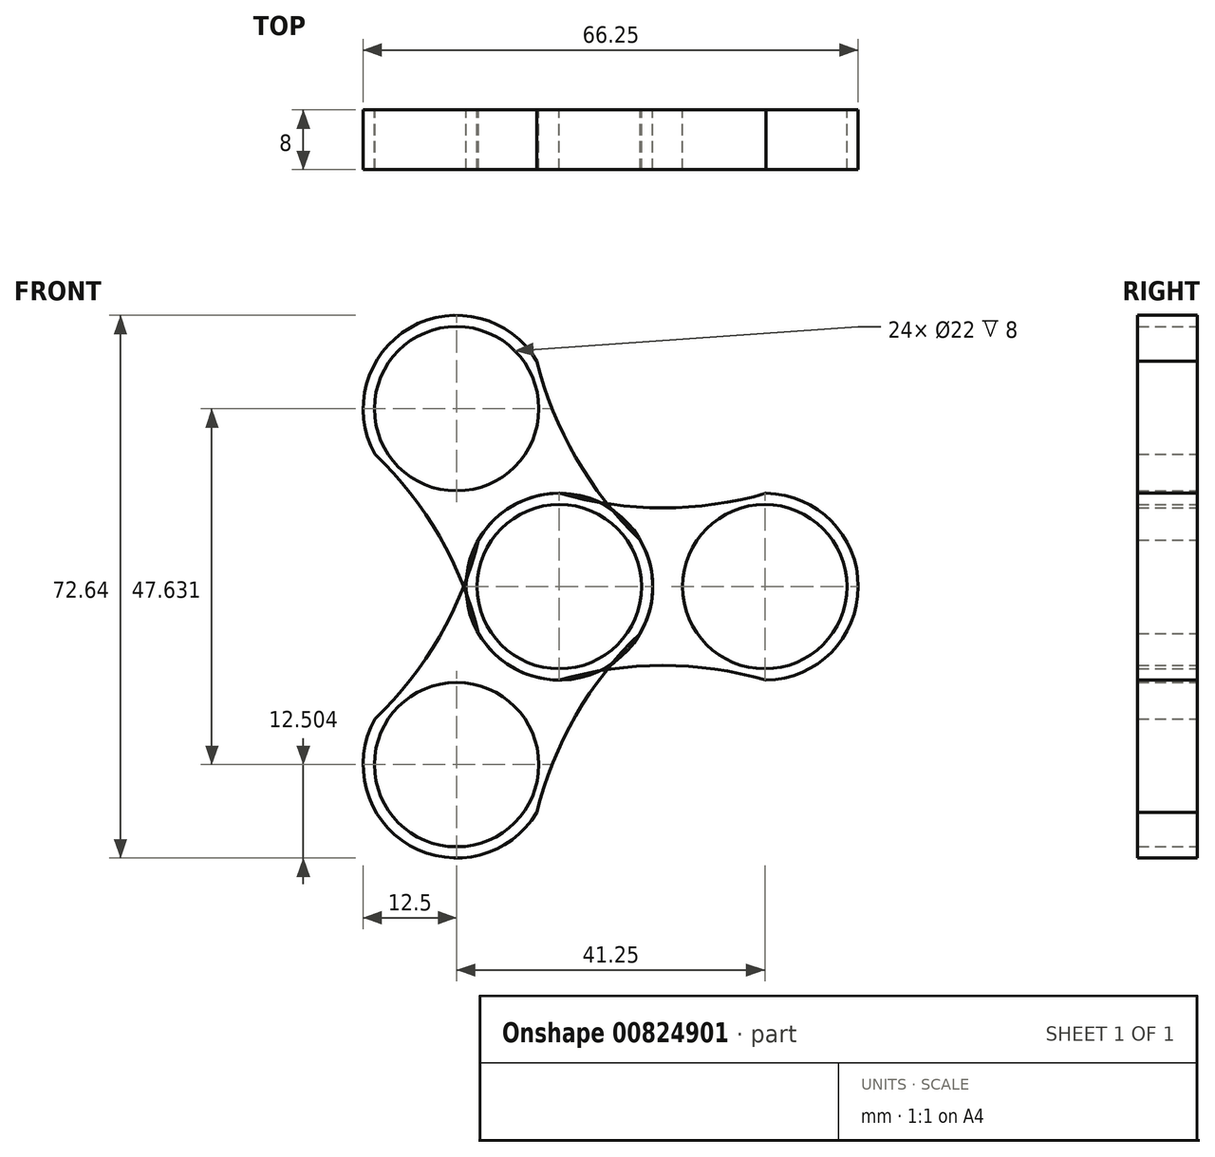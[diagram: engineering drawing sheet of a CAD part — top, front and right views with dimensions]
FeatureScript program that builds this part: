
annotation { "Feature Type Name" : "Feature", "Feature Type Description" : "" }
export const myFeature = defineFeature(function(context is Context, id is Id, definition is map)
    precondition{}
    {
        {
            var Q0;
            Q0=qCreatedBy(makeId("Front.planeOp"),FACE);
            var sketch = newSketch(context, id + "F0", { "sketchPlane" : qUnion([Q0])});
            skCircle(sketch, "E0", {"center": v(0, 0) * mm, "radius": 12.5 * mm});
            skCircle(sketch, "E1", {"center": v(0, 0) * mm, "radius": 11 * mm});
            skCircle(sketch, "E2", {"center": v(27.5, 0) * mm, "radius": 12.5 * mm});
            skCircle(sketch, "E3", {"center": v(27.5, 0) * mm, "radius": 11 * mm});
            skArc(sketch, "E4", {"start": v(0, 12.5) * mm, "mid": v(13.84, 10.55) * mm, "end": v(27.68, 12.5) * mm});
            skArc(sketch, "E5", {"start": v(27.66, -12.5) * mm, "mid": v(13.83, -10.55) * mm, "end": v(0, -12.5) * mm});
            skSolve(sketch);
        }
        {
            var Q0;
            Q0=makeQuery(id+"F0.imprint","IMPRINT",FACE,{"disambiguationData":[TD([[makeQuery(id+"F0.imprint","IMPRINT",EDGE,{"derivedFrom":sQuery(id+"F0.wireOp",EDGE,"E1")}),-1.0]])]});
            var Q1;
            {var subQ0=sQuery(id+"F0.wireOp",EDGE,"E4");var subQ1=sQuery(id+"F0.wireOp",EDGE,"E0");var subQ2=makeQuery(id+"F0.imprint","INTERSECT",VERTEX,{"disambiguationData":[OD(1.0)],"derivedFrom":[subQ1,subQ0]});Q1=makeQuery(id+"F0.imprint","IMPRINT",FACE,{"disambiguationData":[TD([[makeQuery(id+"F0.imprint","IMPRINT",EDGE,{"disambiguationData":[TD([[subQ2,1.0]])],"derivedFrom":subQ1}),-1.0]])]});}
            var Q2;
            Q2=makeQuery(id+"F0.imprint","IMPRINT",FACE,{"disambiguationData":[TD([[makeQuery(id+"F0.imprint","IMPRINT",EDGE,{"derivedFrom":sQuery(id+"F0.wireOp",EDGE,"E3")}),-1.0]])]});
            extrude(context, id + "F1", {"entities" : qUnion([Q0, Q1, Q2]), "depth" : 8 * mm, "offsetDistance" : 25 * mm});
        }
        {
            var Q0;
            Q0=qCreatedBy(makeId("Top.planeOp"),FACE);
            var sketch = newSketch(context, id + "F2", { "sketchPlane" : qUnion([Q0])});
            skLineSegment(sketch, "E6", {"start": v(0, 0) * mm, "end": v(0, -45.4) * mm, "construction": true});
            skSolve(sketch);
        }
        {
            var Q0;
            Q0=makeQuery(id+"F1.opExtrude","SWEPT_BODY",BODY,{"disambiguationData":[OSD([sQuery(id+"F0.wireOp",EDGE,"E0"),sQuery(id+"F0.wireOp",EDGE,"E1"),sQuery(id+"F0.wireOp",EDGE,"E2"),sQuery(id+"F0.wireOp",EDGE,"E3"),sQuery(id+"F0.wireOp",EDGE,"E4"),sQuery(id+"F0.wireOp",EDGE,"E5")])]});
            var Q1;
            Q1=sQuery(id+"F2.wireOp",EDGE,"E6");
            circularPattern(context, id + "F3", {"entities" : qUnion([Q0]), "axis" : qUnion([Q1]), "angle" : 360 * degree, "instanceCount" : 3, "equalSpace" : true});
        }
    });
